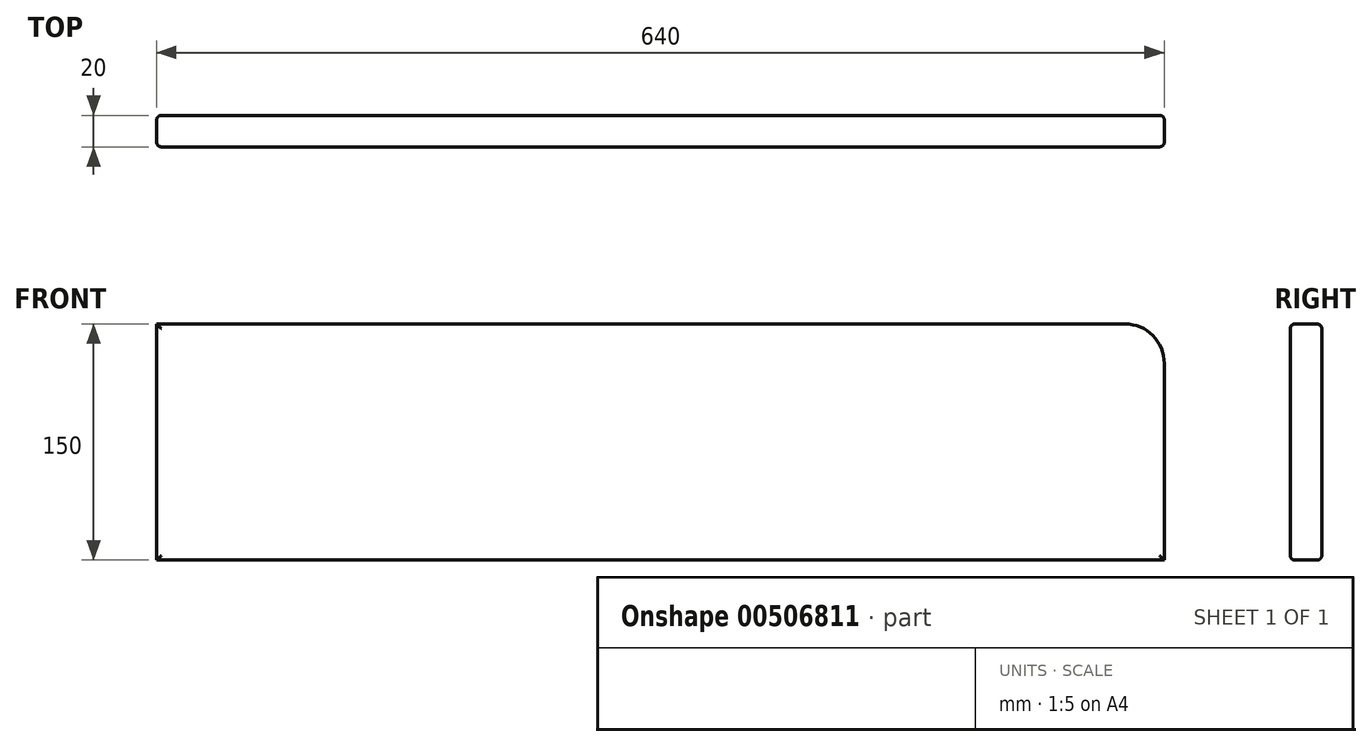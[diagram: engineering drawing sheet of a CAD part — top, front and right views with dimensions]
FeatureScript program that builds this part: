
annotation { "Feature Type Name" : "Feature", "Feature Type Description" : "" }
export const myFeature = defineFeature(function(context is Context, id is Id, definition is map)
    precondition{}
    {
        {
            var Q0;
            Q0=qCreatedBy(makeId("Front.planeOp"),FACE);
            var sketch = newSketch(context, id + "F0", { "sketchPlane" : qUnion([Q0])});
            skLineSegment(sketch, "E0.bottom", {"start": v(-380.07, -45.82) * mm, "end": v(234.93, -45.82) * mm});
            skLineSegment(sketch, "E0.top", {"start": v(-380.07, -195.82) * mm, "end": v(259.93, -195.82) * mm});
            skLineSegment(sketch, "E0.left", {"start": v(-380.07, -45.82) * mm, "end": v(-380.07, -195.82) * mm});
            skLineSegment(sketch, "E0.right", {"start": v(259.93, -70.82) * mm, "end": v(259.93, -195.82) * mm});
            skPoint(sketch, "E1.visualSharp", {"position": v(259.93, -45.82) * mm});
            skArc(sketch, "E1.filletArc", {"start": v(259.93, -70.82) * mm, "mid": v(252.6, -53.15) * mm, "end": v(234.93, -45.82) * mm});
            skSolve(sketch);
        }
        {
            var Q0;
            Q0=makeQuery(id+"F0.imprint","IMPRINT",FACE,{"disambiguationData":[TD([[makeQuery(id+"F0.imprint","IMPRINT",EDGE,{"derivedFrom":sQuery(id+"F0.wireOp",EDGE,"E0.bottom")}),-1.0]])]});
            extrude(context, id + "F1", {"entities" : qUnion([Q0]), "depth" : 20 * mm});
        }
        {
            var Q0;
            Q0=makeQuery(id+"F1.opExtrude","CAP_FACE",FACE,{"disambiguationData":[OSD([sQuery(id+"F0.wireOp",EDGE,"E0.bottom"),sQuery(id+"F0.wireOp",EDGE,"E0.top"),sQuery(id+"F0.wireOp",EDGE,"E0.left"),sQuery(id+"F0.wireOp",EDGE,"E0.right")])],"isStart":true});
            var sketch = newSketch(context, id + "F2", { "sketchPlane" : qUnion([Q0])});
            skLineSegment(sketch, "E2", {"start": v(-259.93, -195.82) * mm, "end": v(-259.93, -165.82) * mm});
            skLineSegment(sketch, "E3", {"start": v(-259.93, -165.82) * mm, "end": v(-204.93, -165.82) * mm});
            skLineSegment(sketch, "E4", {"start": v(-204.93, -165.82) * mm, "end": v(365.07, -165.82) * mm});
            skLineSegment(sketch, "E5", {"start": v(365.07, -165.82) * mm, "end": v(380.07, -165.82) * mm});
            skLineSegment(sketch, "E6", {"start": v(-234.93, -45.82) * mm, "end": v(-234.93, -85.82) * mm});
            skLineSegment(sketch, "E7", {"start": v(-234.93, -85.82) * mm, "end": v(-234.93, -165.82) * mm});
            skSolve(sketch);
        }
        {
            var Q0;
            Q0=makeQuery(id+"F1.opExtrude","CAP_FACE",FACE,{"disambiguationData":[OSD([sQuery(id+"F0.wireOp",EDGE,"E0.bottom"),sQuery(id+"F0.wireOp",EDGE,"E0.top"),sQuery(id+"F0.wireOp",EDGE,"E0.left"),sQuery(id+"F0.wireOp",EDGE,"E0.right")])],"isStart":true});
            var Q1;
            Q1=makeQuery(id+"F1.opExtrude","CAP_FACE",FACE,{"disambiguationData":[OSD([sQuery(id+"F0.wireOp",EDGE,"E0.bottom"),sQuery(id+"F0.wireOp",EDGE,"E0.top"),sQuery(id+"F0.wireOp",EDGE,"E0.left"),sQuery(id+"F0.wireOp",EDGE,"E0.right")])],"isStart":false});
            fillet(context, id + "F3", {"entities" : qUnion([Q0, Q1]), "radius" : 3 * mm, "tangentPropagation" : true, "allowEdgeOverflow" : false});
        }
    });
